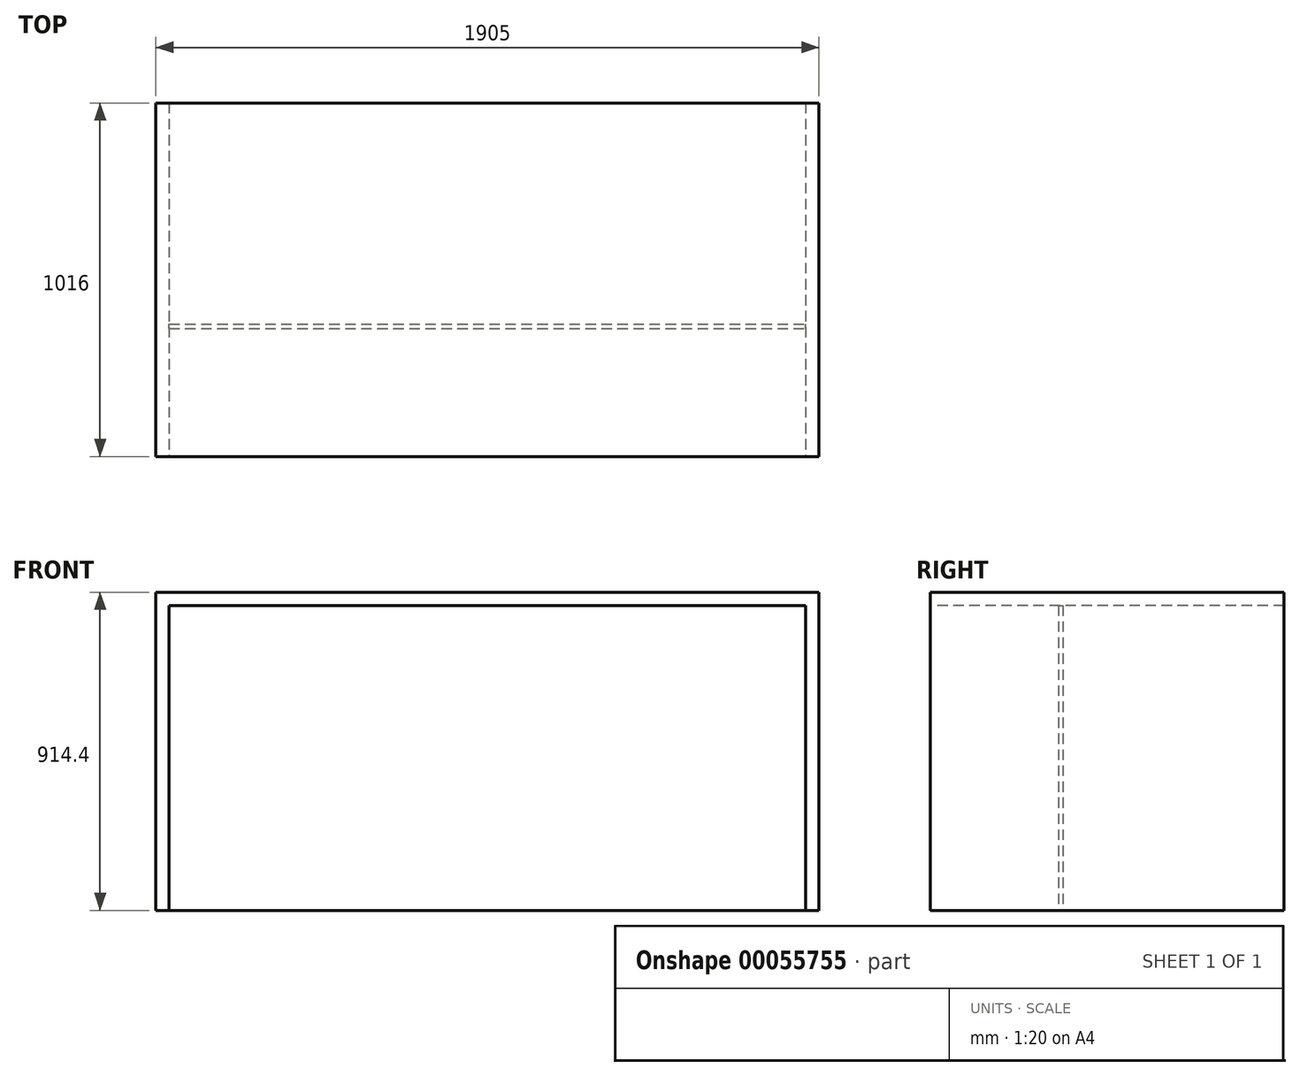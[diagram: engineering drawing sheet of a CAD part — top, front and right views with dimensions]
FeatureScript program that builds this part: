
annotation { "Feature Type Name" : "Feature", "Feature Type Description" : "" }
export const myFeature = defineFeature(function(context is Context, id is Id, definition is map)
    precondition{}
    {
        {
            var Q0;
            Q0=qCreatedBy(makeId("Top.planeOp"),FACE);
            var sketch = newSketch(context, id + "F0", { "sketchPlane" : qUnion([Q0])});
            skLineSegment(sketch, "E0.rect.bottom", {"start": v(914.4, 508) * mm, "end": v(-914.4, 508) * mm});
            skLineSegment(sketch, "E0.rect.top", {"start": v(914.4, -508) * mm, "end": v(-914.4, -508) * mm});
            skLineSegment(sketch, "E0.rect.left", {"start": v(914.4, 508) * mm, "end": v(914.4, -508) * mm});
            skLineSegment(sketch, "E0.rect.right", {"start": v(-914.4, 508) * mm, "end": v(-914.4, -508) * mm});
            skPoint(sketch, "E0.rect.middle", {"position": v(0, 0) * mm});
            skLineSegment(sketch, "E1.bottom", {"start": v(-914.4, 508) * mm, "end": v(-952.5, 508) * mm});
            skLineSegment(sketch, "E1.top", {"start": v(-914.4, -508) * mm, "end": v(-952.5, -508) * mm});
            skLineSegment(sketch, "E1.right", {"start": v(-952.5, 508) * mm, "end": v(-952.5, -508) * mm});
            skLineSegment(sketch, "E2.bottom", {"start": v(914.4, 508) * mm, "end": v(952.5, 508) * mm});
            skLineSegment(sketch, "E2.top", {"start": v(914.4, -508) * mm, "end": v(952.5, -508) * mm});
            skLineSegment(sketch, "E2.right", {"start": v(952.5, 508) * mm, "end": v(952.5, -508) * mm});
            skSolve(sketch);
        }
        {
            var Q0;
            Q0=makeQuery(id+"F0.imprint","IMPRINT",FACE,{"disambiguationData":[TD([[makeQuery(id+"F0.imprint","IMPRINT",EDGE,{"derivedFrom":sQuery(id+"F0.wireOp",EDGE,"E1.bottom")}),1.0]])]});
            var Q1;
            Q1=makeQuery(id+"F0.imprint","IMPRINT",FACE,{"disambiguationData":[TD([[makeQuery(id+"F0.imprint","IMPRINT",EDGE,{"derivedFrom":sQuery(id+"F0.wireOp",EDGE,"E0.rect.bottom")}),1.0]])]});
            var Q2;
            Q2=makeQuery(id+"F0.imprint","IMPRINT",FACE,{"disambiguationData":[TD([[makeQuery(id+"F0.imprint","IMPRINT",EDGE,{"derivedFrom":sQuery(id+"F0.wireOp",EDGE,"E2.bottom")}),-1.0]])]});
            extrude(context, id + "F1", {"entities" : qUnion([Q0, Q1, Q2]), "depth" : 38.1 * mm});
        }
        {
            var Q0;
            Q0=makeQuery(id+"F0.imprint","IMPRINT",FACE,{"disambiguationData":[TD([[makeQuery(id+"F0.imprint","IMPRINT",EDGE,{"derivedFrom":sQuery(id+"F0.wireOp",EDGE,"E1.bottom")}),1.0]])]});
            var Q1;
            Q1=makeQuery(id+"F0.imprint","IMPRINT",FACE,{"disambiguationData":[TD([[makeQuery(id+"F0.imprint","IMPRINT",EDGE,{"derivedFrom":sQuery(id+"F0.wireOp",EDGE,"E2.bottom")}),-1.0]])]});
            extrude(context, id + "F2", {"entities" : qUnion([Q0, Q1]), "operationType" : NewBodyOperationType.ADD, "oppositeDirection" : true, "depth" : 876.3 * mm});
        }
        {
            var Q0;
            {var subQ0=sQuery(id+"F0.wireOp",EDGE,"E2.top");var subQ1=sQuery(id+"F0.wireOp",EDGE,"E1.top");Q0=makeQuery(id+"F2.boolean.opBoolean","MERGE",FACE,{"derivedFrom":[makeQuery(id+"F1.opExtrude","SWEPT_FACE",FACE,{"disambiguationData":[OSD([sQuery(id+"F0.wireOp",EDGE,"E0.rect.top"),subQ1,subQ0])]}),makeQuery(id+"F2.opExtrude","SWEPT_FACE",FACE,{"disambiguationData":[OSD([subQ1])]}),makeQuery(id+"F2.opExtrude","SWEPT_FACE",FACE,{"disambiguationData":[OSD([subQ0])]})]});}
            cPlane(context, id + "F3", {"entities" : qUnion([Q0]), "cplaneType" : CPlaneType.OFFSET, "offset" : 381 * mm, "oppositeDirection" : true, "width" : 152.4 * mm, "height" : 152.4 * mm});
        }
        {
            var Q0;
            Q0=qCreatedBy(id+"F3.planeOp",FACE);
            var sketch = newSketch(context, id + "F4", { "sketchPlane" : qUnion([Q0])});
            skLineSegment(sketch, "E3.bottom", {"start": v(-914.4, 0) * mm, "end": v(914.4, 0) * mm});
            skLineSegment(sketch, "E3.top", {"start": v(-914.4, -876.3) * mm, "end": v(914.4, -876.3) * mm});
            skLineSegment(sketch, "E3.left", {"start": v(-914.4, 0) * mm, "end": v(-914.4, -876.3) * mm});
            skLineSegment(sketch, "E3.right", {"start": v(914.4, 0) * mm, "end": v(914.4, -876.3) * mm});
            skSolve(sketch);
        }
        {
            var Q0;
            Q0=qSketchRegion(id+"F4",true);
            extrude(context, id + "F5", {"entities" : qUnion([Q0]), "depth" : 12.7 * mm});
        }
    });
